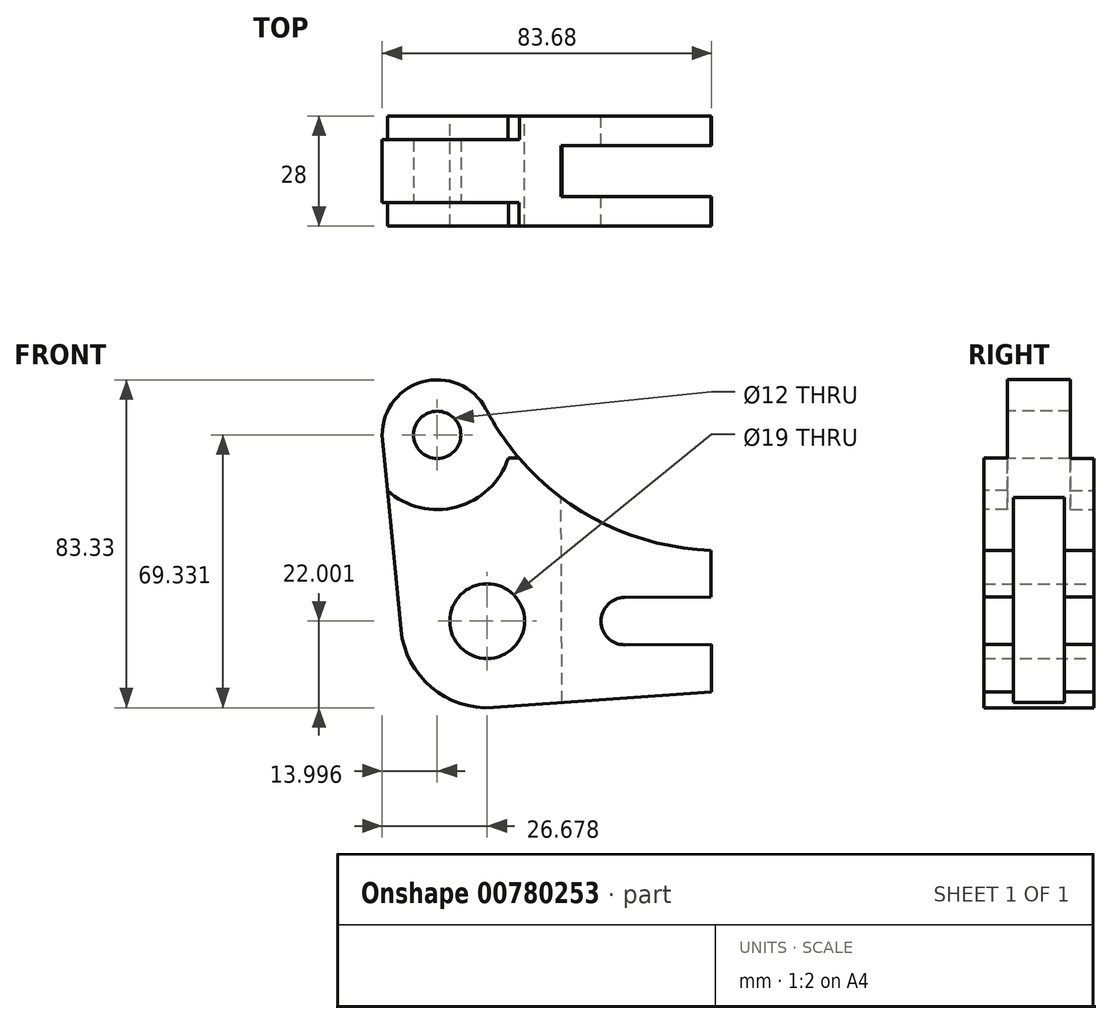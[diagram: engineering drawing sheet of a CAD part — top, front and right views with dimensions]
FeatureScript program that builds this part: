
annotation { "Feature Type Name" : "Feature", "Feature Type Description" : "" }
export const myFeature = defineFeature(function(context is Context, id is Id, definition is map)
    precondition{}
    {
        {
            var Q0;
            Q0=qCreatedBy(makeId("Front.planeOp"),FACE);
            var sketch = newSketch(context, id + "F0", { "sketchPlane" : qUnion([Q0])});
            skLineSegment(sketch, "E0.right", {"start": v(55.28, -7.58) * mm, "end": v(55.33, -19.48) * mm});
            skPoint(sketch, "E0.middle", {"position": v(0, 0) * mm});
            skPoint(sketch, "E1.visualSharp", {"position": v(-55.07, -39.15) * mm});
            skArc(sketch, "E2", {"start": v(-1.85, 28.26) * mm, "mid": v(21.88, 2.63) * mm, "end": v(55.28, -7.58) * mm});
            skArc(sketch, "E3", {"start": v(-1.85, 28.26) * mm, "mid": v(-18.25, 35.16) * mm, "end": v(-28.18, 20.38) * mm});
            skPoint(sketch, "E4.orphan", {"position": v(-55.44, 43.58) * mm});
            skPoint(sketch, "E5.orphan", {"position": v(55.07, 39.15) * mm});
            skPoint(sketch, "E1.filletArc.center.orphan", {"position": v(-1.56, -25.58) * mm});
            skLineSegment(sketch, "E6", {"start": v(-28.18, 20.38) * mm, "end": v(-23.46, -27.73) * mm});
            skArc(sketch, "E7", {"start": v(-23.46, -27.73) * mm, "mid": v(-15.75, -42.4) * mm, "end": v(0, -47.52) * mm});
            skLineSegment(sketch, "E8", {"start": v(55.44, -43.58) * mm, "end": v(0, -47.52) * mm});
            skCircle(sketch, "E9", {"center": v(-1.56, -25.58) * mm, "radius": 9.5 * mm});
            skArc(sketch, "E10", {"start": v(33.33, -19.58) * mm, "mid": v(27.36, -25.6) * mm, "end": v(33.38, -31.58) * mm});
            skLineSegment(sketch, "E11", {"start": v(33.33, -19.58) * mm, "end": v(55.33, -19.48) * mm});
            skLineSegment(sketch, "E12", {"start": v(33.38, -31.58) * mm, "end": v(55.38, -31.48) * mm});
            skLineSegment(sketch, "E13.trimOffspring", {"start": v(55.38, -31.48) * mm, "end": v(55.44, -43.58) * mm});
            skSolve(sketch);
        }
        {
            var Q0;
            Q0 = qSketchRegion(id + "F0", true);
            extrude(context, id + "F1", {"entities" : qUnion([Q0]), "depth" : 28 * mm, "offsetDistance" : 25.4 * mm});
        }
        {
            var Q0;
            Q0=makeQuery(id+"F1.opExtrude","CAP_FACE",FACE,{"disambiguationData":[OSD([sQuery(id+"F0.wireOp",EDGE,"E0.right"),sQuery(id+"F0.wireOp",EDGE,"E2"),sQuery(id+"F0.wireOp",EDGE,"E3"),sQuery(id+"F0.wireOp",EDGE,"E6"),sQuery(id+"F0.wireOp",EDGE,"E7"),sQuery(id+"F0.wireOp",EDGE,"E8"),sQuery(id+"F0.wireOp",EDGE,"E9"),sQuery(id+"F0.wireOp",EDGE,"E10"),sQuery(id+"F0.wireOp",EDGE,"E11"),sQuery(id+"F0.wireOp",EDGE,"E12"),sQuery(id+"F0.wireOp",EDGE,"E13.trimOffspring")])],"isStart":false});
            var sketch = newSketch(context, id + "F2", { "sketchPlane" : qUnion([Q0])});
            skCircle(sketch, "E14", {"center": v(-14.24, 21.75) * mm, "radius": 19 * mm});
            skLineSegment(sketch, "E15", {"start": v(-3.02, 15.8) * mm, "end": v(21.66, 15.91) * mm});
            skSolve(sketch);
        }
        {
            var Q0;
            {var subQ5=makeQuery(id+"F1.opExtrude","CAP_EDGE",EDGE,{"disambiguationData":[OSD([sQuery(id+"F0.wireOp",EDGE,"E3")])],"isStart":false});Q0=makeQuery(id+"F2.imprint","IMPRINT",FACE,{"disambiguationData":[TD([[makeQuery(id+"F2.imprint","IMPRINT",EDGE,{"derivedFrom":subQ5}),-1.0]])]});}
            var Q1;
            {var subQ0=sQuery(id+"F2.wireOp",EDGE,"E15");var subQ1=sQuery(id+"F2.wireOp",EDGE,"E14");var subQ2=makeQuery(id+"F2.imprint","INTERSECT",VERTEX,{"derivedFrom":[subQ1,subQ0]});Q1=makeQuery(id+"F2.imprint","IMPRINT",FACE,{"disambiguationData":[TD([[makeQuery(id+"F2.imprint","IMPRINT",EDGE,{"disambiguationData":[TD([[subQ2,-1.0]])],"derivedFrom":subQ1}),-1.0]])]});}
            var Q2;
            {var subQ0=makeQuery(id+"F1.opExtrude","CAP_EDGE",EDGE,{"disambiguationData":[OSD([sQuery(id+"F0.wireOp",EDGE,"E3")])],"isStart":false});Q2=makeQuery(id+"F2.imprint","IMPRINT",FACE,{"disambiguationData":[TD([[makeQuery(id+"F2.imprint","IMPRINT",EDGE,{"derivedFrom":subQ0}),1.0]])]});}
            extrude(context, id + "F3", {"entities" : qUnion([Q0, Q1, Q2]), "operationType" : NewBodyOperationType.REMOVE, "oppositeDirection" : true, "depth" : 6 * mm, "offsetDistance" : 25.4 * mm});
        }
        {
            var Q0;
            Q0=makeQuery(id+"F3.boolean.opBoolean","COPY",FACE,{"derivedFrom":makeQuery(id+"F3.opExtrude","CAP_FACE",FACE,{"disambiguationData":[OSD([sQuery(id+"F2.wireOp",EDGE,"E14")])],"isStart":false})});
            var sketch = newSketch(context, id + "F4", { "sketchPlane" : qUnion([Q0])});
            skSolve(sketch);
        }
        {
            var Q0;
            {var subQ0=sQuery(id+"F2.wireOp",EDGE,"E14");Q0=makeQuery(id+"F4.imprint","IMPRINT",FACE,{"disambiguationData":[TD([[makeQuery(id+"F4.imprint","IMPRINT",EDGE,{"derivedFrom":makeQuery(id+"F3.boolean.opBoolean","COPY",EDGE,{"derivedFrom":makeQuery(id+"F3.opExtrude","CAP_EDGE",EDGE,{"disambiguationData":[OSD([subQ0])],"isStart":false})})}),1.0]])]});}
            var sketch = newSketch(context, id + "F5", { "sketchPlane" : qUnion([Q0])});
            skCircle(sketch, "E16", {"center": v(-14.24, 21.75) * mm, "radius": 6 * mm});
            skSolve(sketch);
        }
        {
            var Q0;
            Q0 = qSketchRegion(id + "F5", true);
            extrude(context, id + "F6", {"entities" : qUnion([Q0]), "operationType" : NewBodyOperationType.REMOVE, "endBound" : BoundingType.THROUGH_ALL, "oppositeDirection" : true, "depth" : 25.4 * mm, "offsetDistance" : 25.4 * mm});
        }
        {
            var Q0;
            Q0=makeQuery(id+"F1.opExtrude","SWEPT_FACE",FACE,{"disambiguationData":[OSD([sQuery(id+"F0.wireOp",EDGE,"E0.right")])]});
            var sketch = newSketch(context, id + "F7", { "sketchPlane" : qUnion([Q0])});
            skLineSegment(sketch, "E17.bottom", {"start": v(-7.5, -54.53) * mm, "end": v(-20.5, -54.53) * mm});
            skLineSegment(sketch, "E17.top", {"start": v(-7.5, 9.27) * mm, "end": v(-20.5, 9.27) * mm});
            skLineSegment(sketch, "E17.left", {"start": v(-7.5, -54.53) * mm, "end": v(-7.5, 9.27) * mm});
            skLineSegment(sketch, "E17.right", {"start": v(-20.5, -54.53) * mm, "end": v(-20.5, 9.27) * mm});
            skSolve(sketch);
        }
        {
            var Q0;
            Q0 = qSketchRegion(id + "F7", true);
            extrude(context, id + "F8", {"entities" : qUnion([Q0]), "operationType" : NewBodyOperationType.REMOVE, "oppositeDirection" : true, "depth" : 38 * mm, "offsetDistance" : 25.4 * mm});
        }
        {
            var Q0;
            Q0=makeQuery(id+"F1.opExtrude","CAP_FACE",FACE,{"disambiguationData":[OSD([sQuery(id+"F0.wireOp",EDGE,"E0.right"),sQuery(id+"F0.wireOp",EDGE,"E2"),sQuery(id+"F0.wireOp",EDGE,"E3"),sQuery(id+"F0.wireOp",EDGE,"E6"),sQuery(id+"F0.wireOp",EDGE,"E7"),sQuery(id+"F0.wireOp",EDGE,"E8"),sQuery(id+"F0.wireOp",EDGE,"E9"),sQuery(id+"F0.wireOp",EDGE,"E10"),sQuery(id+"F0.wireOp",EDGE,"E11"),sQuery(id+"F0.wireOp",EDGE,"E12"),sQuery(id+"F0.wireOp",EDGE,"E13.trimOffspring")])],"isStart":true});
            var sketch = newSketch(context, id + "F9", { "sketchPlane" : qUnion([Q0])});
            skCircle(sketch, "E18", {"center": v(14.24, 21.75) * mm, "radius": 19 * mm});
            skLineSegment(sketch, "E19", {"start": v(-55.05, 15.75) * mm, "end": v(-3.78, 15.75) * mm});
            skSolve(sketch);
        }
        {
            var Q0;
            Q0 = qSketchRegion(id + "F9", true);
            var Q1;
            {var subQ0=sQuery(id+"F9.wireOp",EDGE,"E19");var subQ1=sQuery(id+"F9.wireOp",EDGE,"E18");var subQ2=makeQuery(id+"F9.imprint","INTERSECT",VERTEX,{"derivedFrom":[subQ1,subQ0]});Q1=makeQuery(id+"F9.imprint","IMPRINT",FACE,{"disambiguationData":[TD([[makeQuery(id+"F9.imprint","IMPRINT",EDGE,{"disambiguationData":[TD([[subQ2,1.0]])],"derivedFrom":subQ1}),-1.0]])]});}
            extrude(context, id + "F10", {"entities" : qUnion([Q0, Q1]), "operationType" : NewBodyOperationType.REMOVE, "oppositeDirection" : true, "depth" : 6 * mm, "offsetDistance" : 25.4 * mm});
        }
    });
